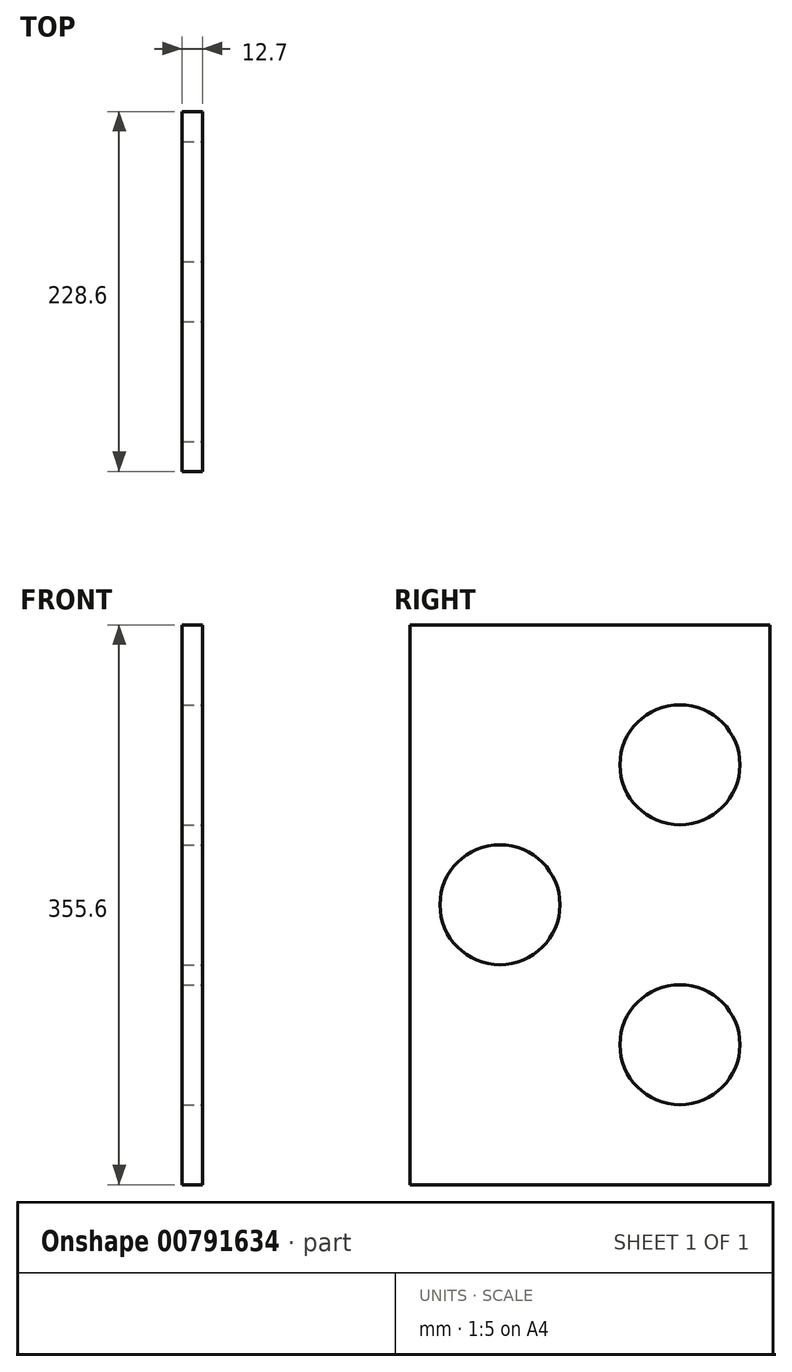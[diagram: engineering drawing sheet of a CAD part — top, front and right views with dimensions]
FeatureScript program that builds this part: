
annotation { "Feature Type Name" : "Feature", "Feature Type Description" : "" }
export const myFeature = defineFeature(function(context is Context, id is Id, definition is map)
    precondition{}
    {
        {
            var Q0;
            Q0=qCreatedBy(makeId("Right.planeOp"),FACE);
            var sketch = newSketch(context, id + "F0", { "sketchPlane" : qUnion([Q0])});
            skLineSegment(sketch, "E0.bottom", {"start": v(-114.3, 177.8) * mm, "end": v(114.3, 177.8) * mm});
            skLineSegment(sketch, "E0.top", {"start": v(-114.3, -177.8) * mm, "end": v(114.3, -177.8) * mm});
            skLineSegment(sketch, "E0.left", {"start": v(-114.3, 177.8) * mm, "end": v(-114.3, -177.8) * mm});
            skLineSegment(sketch, "E0.right", {"start": v(114.3, 177.8) * mm, "end": v(114.3, -177.8) * mm});
            skPoint(sketch, "E0.middle", {"position": v(0, 0) * mm});
            skSolve(sketch);
        }
        {
            var Q0;
            Q0=makeQuery(id+"F0.imprint","IMPRINT",FACE,{"disambiguationData":[TD([[makeQuery(id+"F0.imprint","IMPRINT",EDGE,{"derivedFrom":sQuery(id+"F0.wireOp",EDGE,"E0.bottom")}),-1.0]])]});
            extrude(context, id + "F1", {"entities" : qUnion([Q0]), "depth" : 12.7 * mm, "offsetDistance" : 25.4 * mm});
        }
        {
            var Q0;
            Q0=makeQuery(id+"F1.opExtrude","CAP_FACE",FACE,{"disambiguationData":[OSD([sQuery(id+"F0.wireOp",EDGE,"E0.bottom"),sQuery(id+"F0.wireOp",EDGE,"E0.top"),sQuery(id+"F0.wireOp",EDGE,"E0.left"),sQuery(id+"F0.wireOp",EDGE,"E0.right")])],"isStart":false});
            var sketch = newSketch(context, id + "F2", { "sketchPlane" : qUnion([Q0])});
            skCircle(sketch, "E1", {"center": v(-57.15, 0) * mm, "radius": 38.1 * mm});
            skCircle(sketch, "E2", {"center": v(57.15, 88.9) * mm, "radius": 38.1 * mm});
            skCircle(sketch, "E3", {"center": v(57.15, -88.9) * mm, "radius": 38.1 * mm});
            skSolve(sketch);
        }
        {
            var Q0;
            Q0=sQuery(id+"F2.wireOp",VERTEX,"E3.center");
            var Q1;
            Q1=sQuery(id+"F2.wireOp",VERTEX,"E1.center");
            var Q2;
            Q2=sQuery(id+"F2.wireOp",VERTEX,"E2.center");
            var Q3;
            Q3=makeQuery(id+"F1.opExtrude","SWEPT_BODY",BODY,{"disambiguationData":[OSD([sQuery(id+"F0.wireOp",EDGE,"E0.bottom"),sQuery(id+"F0.wireOp",EDGE,"E0.top"),sQuery(id+"F0.wireOp",EDGE,"E0.left"),sQuery(id+"F0.wireOp",EDGE,"E0.right")])]});
            hole(context, id + "F3", {"style" : HoleStyle.SIMPLE, "endStyle" : HoleEndStyle.THROUGH, "holeDiameter" : 76.2 * mm, "majorDiameter" : 6.35 * mm, "isTappedThrough" : true, "tappedDepth" : 12.7 * mm, "tapClearance" : 3, "locations" : qUnion([Q0, Q1, Q2]), "scope" : qUnion([Q3])});
        }
    });
